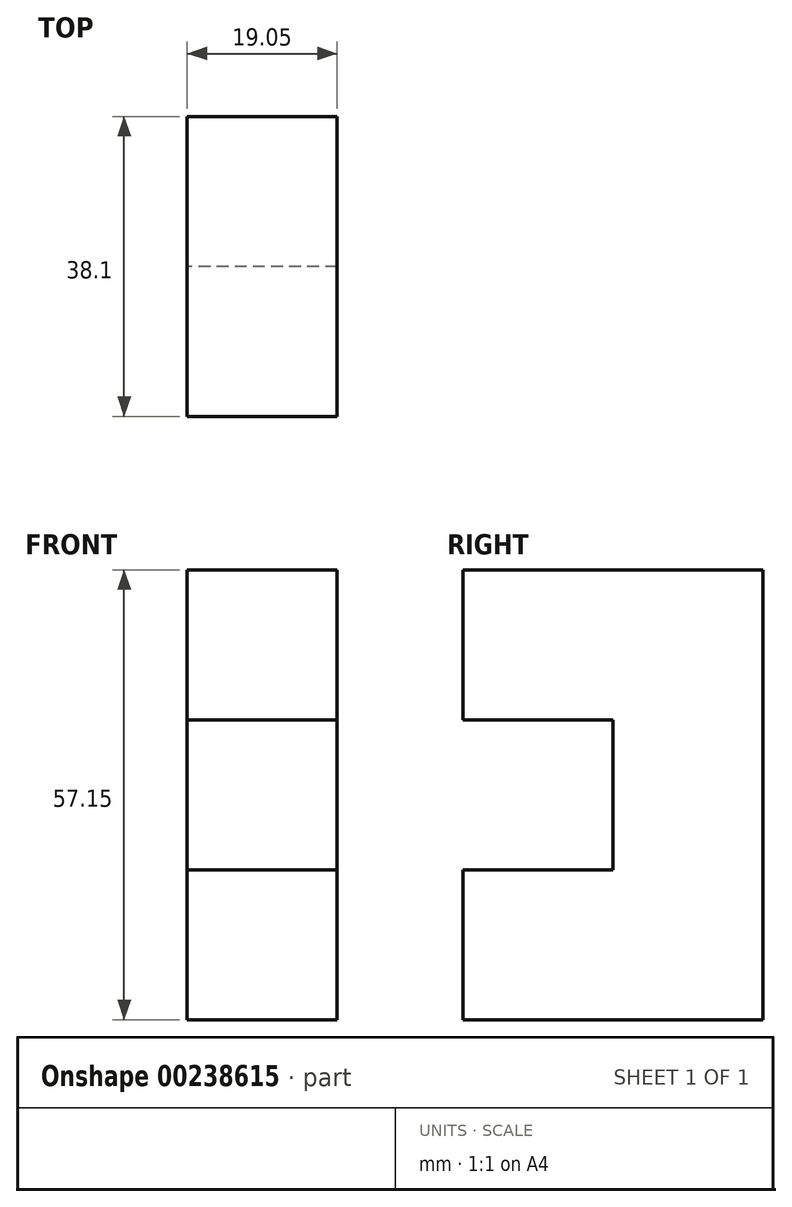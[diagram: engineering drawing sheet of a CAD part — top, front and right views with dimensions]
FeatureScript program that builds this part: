
annotation { "Feature Type Name" : "Feature", "Feature Type Description" : "" }
export const myFeature = defineFeature(function(context is Context, id is Id, definition is map)
    precondition{}
    {
        {
            var Q0;
            Q0=qCreatedBy(makeId("Right.planeOp"),FACE);
            var sketch = newSketch(context, id + "F0", { "sketchPlane" : qUnion([Q0])});
            skLineSegment(sketch, "E0", {"start": v(0, 0) * mm, "end": v(0, 19.05) * mm});
            skLineSegment(sketch, "E1", {"start": v(0, 19.05) * mm, "end": v(38.1, 19.05) * mm});
            skLineSegment(sketch, "E2", {"start": v(38.1, 19.05) * mm, "end": v(38.1, -38.1) * mm});
            skLineSegment(sketch, "E3", {"start": v(38.1, -38.1) * mm, "end": v(0, -38.1) * mm});
            skLineSegment(sketch, "E4", {"start": v(0, -38.1) * mm, "end": v(0, -19.05) * mm});
            skLineSegment(sketch, "E5", {"start": v(0, -19.05) * mm, "end": v(19.05, -19.05) * mm});
            skLineSegment(sketch, "E6", {"start": v(19.05, -19.05) * mm, "end": v(19.05, 0) * mm});
            skLineSegment(sketch, "E7", {"start": v(19.05, 0) * mm, "end": v(0, 0) * mm});
            skSolve(sketch);
        }
        {
            var Q0;
            Q0=makeQuery(id+"F0.imprint","IMPRINT",FACE,{"disambiguationData":[TD([[makeQuery(id+"F0.imprint","IMPRINT",EDGE,{"derivedFrom":sQuery(id+"F0.wireOp",EDGE,"E0")}),-1.0]])]});
            extrude(context, id + "F1", {"entities" : qUnion([Q0]), "depth" : 19.05 * mm});
        }
    });
